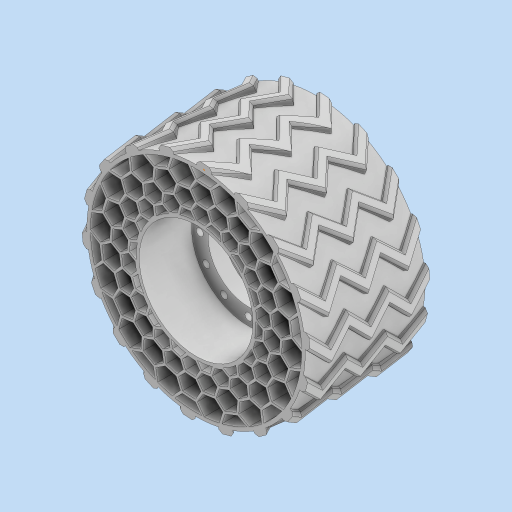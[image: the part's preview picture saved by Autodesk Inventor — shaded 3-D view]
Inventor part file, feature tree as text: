
AUTODESK INVENTOR PART (.ipt)
format: ipt  version: 2023 (Build 270158000, 158)  size: 1,183,232 bytes
history: native  units: in
note: dims shown in document units (in); Inventor stores cm internally (conversion verified against a paired STEP export)
features: extrude x21, other x18, thicken_offset x17, sketch x5, pattern_circular x2, plane x2, mirror x1, sweep x1
ambient origin geometry x8: Origin, YZ Plane, XZ Plane, XY Plane, X Axis, Y Axis, Z Axis, Center Point
bodies: Solid1 (feature_tree)
feature tree (67):
  sketch  "Sketch1"  dims[d0=3.1496in d1=0.0in d2=3.1496in d3=0.0in]
  extrude  "Extrusion1"  Depth=3.1496in TaperAngle=0.0deg
  thicken_offset  "Thicken1"
  thicken_offset  "Thicken2"
  thicken_offset  "Thicken3"
  thicken_offset  "Thicken4"
  thicken_offset  "Thicken5"
  thicken_offset  "Thicken6"
  thicken_offset  "Thicken7"
  thicken_offset  "Thicken8"
  thicken_offset  "Thicken9"
  thicken_offset  "Thicken10"
  thicken_offset  "Thicken11"
  thicken_offset  "Thicken12"
  thicken_offset  "Thicken13"
  thicken_offset  "Thicken14"
  thicken_offset  "Thicken15"
  thicken_offset  "Thicken16"
  thicken_offset  "Thicken17"
  pattern_circular  "Circular Pattern1"  Count=8  [1 undecoded]
  sketch  "Sketch2"  dims[d4=0.0945in d5=3.1496in d6=0.0in]
  extrude  "Extrusion2"  Depth=3.1496in TaperAngle=0.0deg
  plane  "Work Plane1"
  mirror  "Mirror1"
  extrude  "Extrusion3"  Depth=3.1496in TaperAngle=0.0deg
  sketch  "Sketch3"  dims[d7=0.063in d8=3.1496in d9=0.0in]
  other  "Work Point1"
  plane  "Work Plane2"
  sweep  "Sweep1"
  extrude  "Extrusion4"  Depth=0.063in
  pattern_circular  "Circular Pattern2"  Count=8  [1 undecoded]
  other  "Srf1"
  other  "Srf2"
  other  "Srf3"
  other  "Srf4"
  other  "Srf5"
  other  "Srf6"
  other  "Srf7"
  other  "Srf8"
  other  "Srf9"
  other  "Srf10"
  other  "Srf11"
  other  "Srf12"
  other  "Srf13"
  other  "Srf14"
  other  "Srf15"
  other  "Srf16"
  other  "Srf17"
  sketch  "Sketch4"  dims[d10=0.063in d11=3.1496in d12=0.0in]
  sketch  "Sketch5"  dims[d13=0.063in d14=3.1496in d15=0.0in d16=0.063in d17=3.1496in d18=0.0in d19=0.063in d20=3.1496in d21=0.0in d22=0.063in d23=3.1496in d24=0.0in d25=0.063in d26=3.1496in d27=0.0in d28=0.063in d29=3.1496in d30=0.0in d31=0.063in d32=3.1496in d33=0.0in d34=0.063in d35=3.1496in d36=0.0in d37=0.063in d38=3.1496in d39=0.0in d40=0.063in d41=3.1496in d42=0.0in d43=0.063in d44=3.1496in d45=0.0in d46=0.063in d47=3.1496in d48=0.0in d49=0.063in d50=3.1496in d51=0.0in d52=0.063in d53=5.5118in d54=360.0deg d56=0.0787in d57=2.5591in d58=0.19in d59=4.7244in d61=360.0deg d63=1.378in d64=0.0in d65=0.5in d66=0.0in d67=0.0in d68=0.002in d69=0.3937in d70=0.126in d71=0.0787in d72=0.0787in d73=0.0787in d74=0.0787in d75=0.0in d76=0.0in d77=0.0in d78=0.0in d79=7.0866in d80=360.0deg]
  extrude  "ExtrusionSrf1"  Depth=0.063in
  extrude  "ExtrusionSrf2"  Depth=3.1496in TaperAngle=0.0deg
  extrude  "ExtrusionSrf3"  Depth=0.063in
  extrude  "ExtrusionSrf4"  Depth=3.1496in TaperAngle=0.0deg
  extrude  "ExtrusionSrf5"  Depth=0.063in
  extrude  "ExtrusionSrf6"  Depth=3.1496in TaperAngle=0.0deg
  extrude  "ExtrusionSrf7"  Depth=0.063in
  extrude  "ExtrusionSrf8"  Depth=3.1496in TaperAngle=0.0deg
  extrude  "ExtrusionSrf9"  Depth=0.063in
  extrude  "ExtrusionSrf10"  Depth=3.1496in TaperAngle=0.0deg
  extrude  "ExtrusionSrf11"  Depth=0.063in
  extrude  "ExtrusionSrf12"  Depth=3.1496in TaperAngle=0.0deg
  extrude  "ExtrusionSrf13"  Depth=0.063in
  extrude  "ExtrusionSrf14"  Depth=3.1496in TaperAngle=0.0deg
  extrude  "ExtrusionSrf15"  Depth=0.063in
  extrude  "ExtrusionSrf16"  Depth=3.1496in TaperAngle=0.0deg
  extrude  "ExtrusionSrf17"  Depth=0.063in
note: 2 required parameter values undecoded (feature->parameter linkage not recoverable at this tier; creation-order binding heuristic only, values carry confidence <= 0.55)
